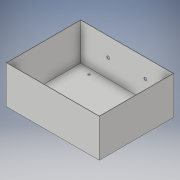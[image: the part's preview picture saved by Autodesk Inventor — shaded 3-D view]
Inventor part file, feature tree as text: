
AUTODESK INVENTOR PART (.ipt)
format: ipt  version: 2018 (Build 220112000, 112)  size: 127,488 bytes
history: native  units: in
note: dims shown in document units (in); Inventor stores cm internally (conversion verified against a paired STEP export)
features: extrude x4, sketch x4
ambient origin geometry x8: Origin, YZ Plane, XZ Plane, XY Plane, X Axis, Y Axis, Z Axis, Center Point
bodies: Solid1 (feature_tree)
feature tree (8):
  extrude  "Extrusion1"  Depth=4.0in
  extrude  "Extrusion2"  Depth=4.96in
  extrude  "Extrusion3"  Depth=2.0in TaperAngle=0.0deg
  extrude  "Extrusion4"  Depth=0.164in
  sketch  "Sketch1"  dims[d0=5.0in d1=4.0in]
  sketch  "Sketch2"  dims[d2=0.04in d3=0.0in d4=4.96in]
  sketch  "Sketch3"  dims[d5=3.96in d6=2.0in d7=0.0in]
  sketch  "Sketch4"  dims[d10=0.164in d12=0.164in d13=0.0in d14=0.0in d15=3.937in d16=3.937in d23=0.112in d24=0.112in d25=0.112in d26=0.0in d27=0.0in]
